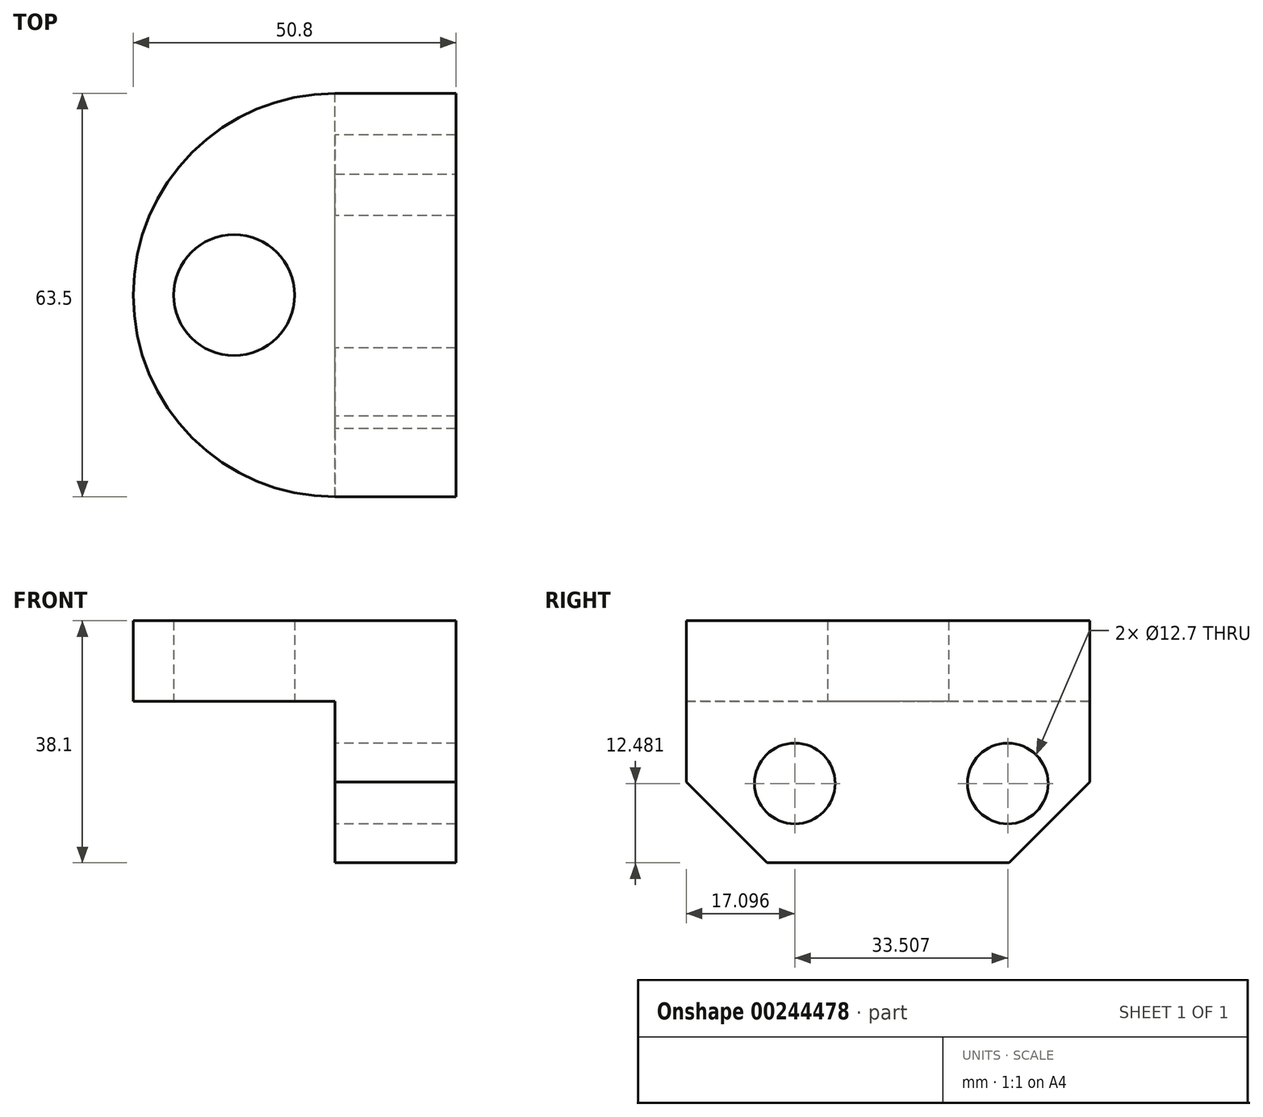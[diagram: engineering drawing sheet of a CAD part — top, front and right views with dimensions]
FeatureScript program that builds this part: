
annotation { "Feature Type Name" : "Feature", "Feature Type Description" : "" }
export const myFeature = defineFeature(function(context is Context, id is Id, definition is map)
    precondition{}
    {
        {
            var Q0;
            Q0=qCreatedBy(makeId("Right.planeOp"),FACE);
            var sketch = newSketch(context, id + "F0", { "sketchPlane" : qUnion([Q0])});
            skLineSegment(sketch, "E0.bottom", {"start": v(-31.75, -19.05) * mm, "end": v(31.75, -19.05) * mm});
            skLineSegment(sketch, "E0.top", {"start": v(-31.75, 19.05) * mm, "end": v(31.75, 19.05) * mm});
            skLineSegment(sketch, "E0.left", {"start": v(-31.75, -19.05) * mm, "end": v(-31.75, 19.05) * mm});
            skLineSegment(sketch, "E0.right", {"start": v(31.75, -19.05) * mm, "end": v(31.75, 19.05) * mm});
            skPoint(sketch, "E0.middle", {"position": v(0, 0) * mm});
            skPoint(sketch, "E1", {"position": v(-14.65, -6.57) * mm});
            skPoint(sketch, "E2", {"position": v(18.85, -6.57) * mm});
            skLineSegment(sketch, "E3", {"start": v(0, 19.05) * mm, "end": v(0, 0) * mm});
            skSolve(sketch);
        }
        {
            var Q0;
            Q0=makeQuery(id+"F0.imprint","IMPRINT",FACE,{"disambiguationData":[TD([[makeQuery(id+"F0.imprint","IMPRINT",EDGE,{"derivedFrom":sQuery(id+"F0.wireOp",EDGE,"E0.bottom")}),1.0]])]});
            extrude(context, id + "F1", {"entities" : qUnion([Q0]), "depth" : 19.05 * mm});
        }
        {
            var Q0;
            Q0=makeQuery(id+"F1.opExtrude","SWEPT_EDGE",EDGE,{"disambiguationData":[OSD([sQuery(id+"F0.wireOp",EDGE,"E0.bottom"),sQuery(id+"F0.wireOp",EDGE,"E0.left")])]});
            chamfer(context, id + "F2", {"entities" : qUnion([Q0]), "width" : 12.7 * mm, "tangentPropagation" : true});
        }
        {
            var Q0;
            Q0=makeQuery(id+"F1.opExtrude","SWEPT_EDGE",EDGE,{"disambiguationData":[OSD([sQuery(id+"F0.wireOp",EDGE,"E0.bottom"),sQuery(id+"F0.wireOp",EDGE,"E0.right")])]});
            chamfer(context, id + "F3", {"entities" : qUnion([Q0]), "width" : 12.7 * mm, "tangentPropagation" : true});
        }
        {
            var Q0;
            Q0=sQuery(id+"F0.wireOp",VERTEX,"E1");
            var Q1;
            Q1=sQuery(id+"F0.wireOp",VERTEX,"E2");
            var Q2;
            Q2=makeQuery(id+"F1.opExtrude","SWEPT_BODY",BODY,{"disambiguationData":[OSD([sQuery(id+"F0.wireOp",EDGE,"E0.bottom"),sQuery(id+"F0.wireOp",EDGE,"E0.top"),sQuery(id+"F0.wireOp",EDGE,"E0.left"),sQuery(id+"F0.wireOp",EDGE,"E0.right")])]});
            hole(context, id + "F4", {"style" : HoleStyle.SIMPLE, "endStyle" : HoleEndStyle.THROUGH, "oppositeDirection" : true, "holeDiameter" : 12.7 * mm, "tappedDepth" : 12.7 * mm, "tapClearance" : 3, "locations" : qUnion([Q0, Q1]), "scope" : qUnion([Q2])});
        }
        {
            var Q0;
            Q0=makeQuery(id+"F1.opExtrude","SWEPT_FACE",FACE,{"disambiguationData":[OSD([sQuery(id+"F0.wireOp",EDGE,"E0.top")])]});
            var sketch = newSketch(context, id + "F5", { "sketchPlane" : qUnion([Q0])});
            skLineSegment(sketch, "E4", {"start": v(19.05, 0) * mm, "end": v(-31.75, 0) * mm});
            skCircle(sketch, "E5", {"center": v(0, 0) * mm, "radius": 31.75 * mm});
            skArc(sketch, "E6", {"start": v(0, -31.75) * mm, "mid": v(-31.75, 0) * mm, "end": v(0, 31.75) * mm});
            skSolve(sketch);
        }
        {
            var Q0;
            {var subQ0=sQuery(id+"F5.wireOp",EDGE,"E5");var subQ1=sQuery(id+"F5.wireOp",EDGE,"E4");var subQ2=makeQuery(id+"F5.imprint","INTERSECT",VERTEX,{"derivedFrom":[subQ1,subQ0]});Q0=makeQuery(id+"F5.imprint","IMPRINT",FACE,{"disambiguationData":[TD([[makeQuery(id+"F5.imprint","IMPRINT",EDGE,{"disambiguationData":[TD([[subQ2,1.0]])],"derivedFrom":subQ1}),1.0]])]});}
            var Q1;
            {var subQ0=sQuery(id+"F5.wireOp",EDGE,"E5");var subQ1=sQuery(id+"F5.wireOp",EDGE,"E4");var subQ2=makeQuery(id+"F5.imprint","INTERSECT",VERTEX,{"derivedFrom":[subQ1,subQ0]});Q1=makeQuery(id+"F5.imprint","IMPRINT",FACE,{"disambiguationData":[TD([[makeQuery(id+"F5.imprint","IMPRINT",EDGE,{"disambiguationData":[TD([[subQ2,1.0]])],"derivedFrom":subQ1}),-1.0]])]});}
            extrude(context, id + "F6", {"entities" : qUnion([Q0, Q1]), "operationType" : NewBodyOperationType.ADD, "oppositeDirection" : true, "depth" : 12.7 * mm});
        }
        {
            var Q0;
            Q0=qCreatedBy(makeId("Top.planeOp"),FACE);
            var sketch = newSketch(context, id + "F7", { "sketchPlane" : qUnion([Q0])});
            skPoint(sketch, "E7", {"position": v(-15.88, 0) * mm});
            skLineSegment(sketch, "E8", {"start": v(0, 0) * mm, "end": v(-15.88, 0) * mm});
            skSolve(sketch);
        }
        {
            var Q0;
            Q0=sQuery(id+"F7.wireOp",VERTEX,"E7");
            var Q1;
            Q1=makeQuery(id+"F1.opExtrude","SWEPT_BODY",BODY,{"disambiguationData":[OSD([sQuery(id+"F0.wireOp",EDGE,"E0.bottom"),sQuery(id+"F0.wireOp",EDGE,"E0.top"),sQuery(id+"F0.wireOp",EDGE,"E0.left"),sQuery(id+"F0.wireOp",EDGE,"E0.right")])]});
            hole(context, id + "F8", {"style" : HoleStyle.SIMPLE, "endStyle" : HoleEndStyle.THROUGH, "oppositeDirection" : true, "holeDiameter" : 19.05 * mm, "tappedDepth" : 12.7 * mm, "tapClearance" : 3, "locations" : qUnion([Q0]), "scope" : qUnion([Q1])});
        }
    });
